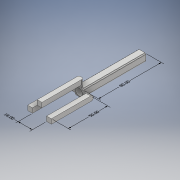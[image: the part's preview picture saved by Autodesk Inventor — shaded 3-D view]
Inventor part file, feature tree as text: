
AUTODESK INVENTOR PART (.ipt)
format: ipt  version: 2018 (Build 220112000, 112)  size: 212,480 bytes
history: native  units: mm
features: extrude x6, sketch x6, other x4, fillet x2, hole x1
ambient origin geometry x8: Origin, YZ Plane, XZ Plane, XY Plane, X Axis, Y Axis, Z Axis, Center Point
bodies: Solide1 (feature_tree)
feature tree (19):
  other  "Annotations"
  extrude  "Extrusion1"  Depth=10.0mm
  hole  "Perçage3"  [1 undecoded]
  fillet  "Congé2"  Radius=10.0mm
  extrude  "Extrusion2"  Depth=2.0mm
  extrude  "Extrusion3"  Depth=3.0mm
  extrude  "Extrusion4"  Depth=10.0mm TaperAngle=0.0deg
  extrude  "Extrusion5"  Depth=3.0mm
  extrude  "Extrusion6"  Depth=10.0mm TaperAngle=0.0deg
  fillet  "Congé3"  Radius=6.0mm
  sketch  "Esquisse1"
  sketch  "Esquisse2"
  sketch  "Esquisse3"
  sketch  "Esquisse4"
  sketch  "Esquisse5"
  sketch  "Esquisse6"
  other  "Cote linéaire 1"
  other  "Cote linéaire 2"
  other  "Cote linéaire 3"
note: 1 required parameter value undecoded (feature->parameter linkage not recoverable at this tier; creation-order binding heuristic only, values carry confidence <= 0.55)
